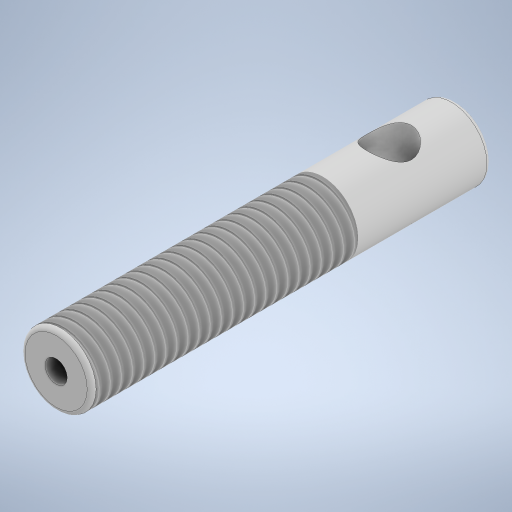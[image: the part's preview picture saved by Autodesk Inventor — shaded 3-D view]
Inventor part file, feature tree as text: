
AUTODESK INVENTOR PART (.ipt)
format: ipt  version: 2023 (Build 270158030, 158C)  size: 298,496 bytes
history: native  units: mm
features: extrude x3, sketch x3, fillet x2, thread x1
ambient origin geometry x8: Origin, YZ Plane, XZ Plane, XY Plane, X Axis, Y Axis, Z Axis, Center Point
bodies: Solid1 (feature_tree)
feature tree (9):
  extrude  "Extrusion1"  Depth=45.0mm TaperAngle=0.0deg
  extrude  "Extrusion2"  Depth=10.0mm TaperAngle=0.0deg
  extrude  "Extrusion3"  Depth=7.5mm
  thread  "Thread1"  [1 undecoded]
  fillet  "Fillet1"  Radius=30.0mm
  fillet  "Fillet2"  Radius=0.5mm
  sketch  "Sketch1"  dims[d0=8.0mm d1=45.0mm d2=0.0mm]
  sketch  "Sketch2"  dims[d3=2.5mm d4=10.0mm d5=0.0mm]
  sketch  "Sketch3"  dims[d6=5.0mm d7=7.5mm d8=10.0mm d9=0.0mm d10=30.0mm d11=15.0mm d12=0.5mm d13=0.5mm]
note: 1 required parameter value undecoded (feature->parameter linkage not recoverable at this tier; creation-order binding heuristic only, values carry confidence <= 0.55)
